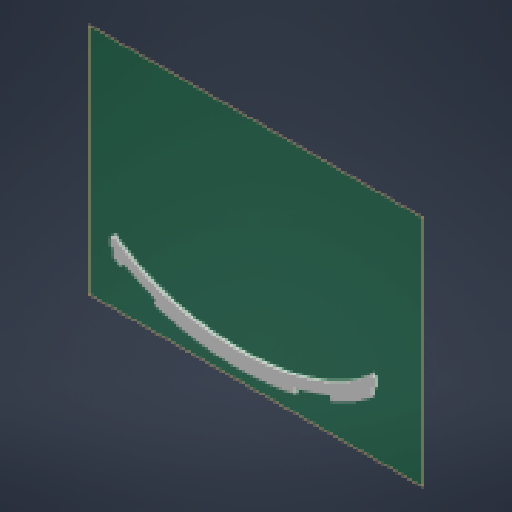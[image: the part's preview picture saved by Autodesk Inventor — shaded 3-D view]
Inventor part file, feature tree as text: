
AUTODESK INVENTOR PART (.ipt)
format: ipt  version: 2023 (Build 270158000, 158)  size: 245,248 bytes
history: native  units: mm
features: extrude x3, sketch x3, other x2, plane x1
ambient origin geometry x8: Origin, YZ Plane, XZ Plane, XY Plane, X Axis, Y Axis, Z Axis, Center Point
bodies: Solid1 (feature_tree)
feature tree (9):
  plane  "Work Plane1"
  extrude  "Extrusion1"  Depth=15.0mm
  extrude  "Extrusion2"  Depth=3.0mm
  extrude  "Extrusion3"  Depth=8.0mm TaperAngle=0.0deg
  sketch  "Sketch1"  dims[d0=15.0mm d1=15.0mm]
  sketch  "Sketch2"  dims[d2=3.0mm d3=0.0mm d4=3.0mm]
  sketch  "Sketch3"  dims[d5=8.0mm d6=3.0mm d7=0.0mm d8=8.0mm d9=3.0mm d10=3.0mm d11=0.0mm]
  other  "Assembly1"
  other  "vase_v2._tom:1"
